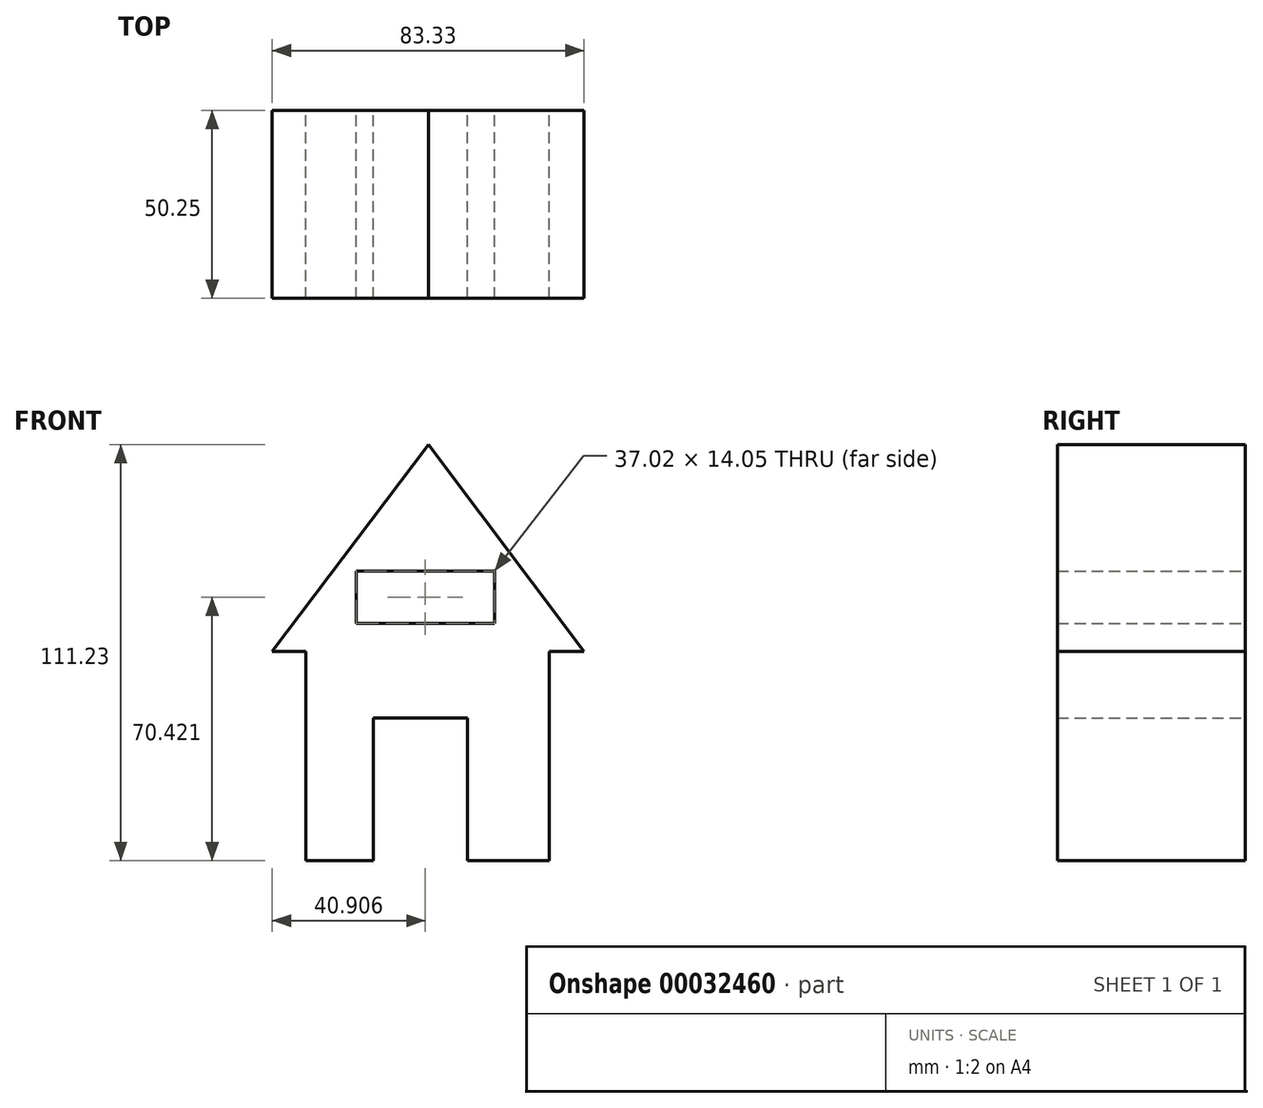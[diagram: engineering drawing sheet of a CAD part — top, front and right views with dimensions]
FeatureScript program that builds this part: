
annotation { "Feature Type Name" : "Feature", "Feature Type Description" : "" }
export const myFeature = defineFeature(function(context is Context, id is Id, definition is map)
    precondition{}
    {
        {
            var Q0;
            Q0=qCreatedBy(makeId("Front.planeOp"),FACE);
            var sketch = newSketch(context, id + "F0", { "sketchPlane" : qUnion([Q0])});
            skLineSegment(sketch, "E0.bottom", {"start": v(-32.84, 0) * mm, "end": v(32.27, 0) * mm});
            skLineSegment(sketch, "E0.top", {"start": v(-32.84, -55.9) * mm, "end": v(32.27, -55.9) * mm});
            skLineSegment(sketch, "E0.left", {"start": v(-32.84, 0) * mm, "end": v(-32.84, -55.9) * mm});
            skLineSegment(sketch, "E0.right", {"start": v(32.27, 0) * mm, "end": v(32.27, -55.9) * mm});
            skLineSegment(sketch, "E1", {"start": v(-41.76, 0) * mm, "end": v(41.57, 0) * mm});
            skLineSegment(sketch, "E2", {"start": v(-41.76, 0) * mm, "end": v(0, 55.33) * mm});
            skLineSegment(sketch, "E3", {"start": v(41.57, 0) * mm, "end": v(0, 55.33) * mm});
            skLineSegment(sketch, "E4", {"start": v(-14.8, -55.9) * mm, "end": v(-14.8, -17.75) * mm});
            skLineSegment(sketch, "E5", {"start": v(-14.8, -17.75) * mm, "end": v(10.44, -17.75) * mm});
            skLineSegment(sketch, "E6", {"start": v(10.44, -17.75) * mm, "end": v(10.44, -55.9) * mm});
            skLineSegment(sketch, "E7.bottom", {"start": v(-19.36, 21.54) * mm, "end": v(17.65, 21.54) * mm});
            skLineSegment(sketch, "E7.top", {"start": v(-19.36, 7.5) * mm, "end": v(17.65, 7.5) * mm});
            skLineSegment(sketch, "E7.left", {"start": v(-19.36, 21.54) * mm, "end": v(-19.36, 7.5) * mm});
            skLineSegment(sketch, "E7.right", {"start": v(17.65, 21.54) * mm, "end": v(17.65, 7.5) * mm});
            skSolve(sketch);
        }
        {
            var Q0;
            {var subQ1=sQuery(id+"F0.wireOp",EDGE,"E2");Q0=makeQuery(id+"F0.imprint","IMPRINT",FACE,{"disambiguationData":[TD([[makeQuery(id+"F0.imprint","IMPRINT",EDGE,{"derivedFrom":subQ1}),-1.0]])]});}
            var Q1;
            {var subQ3=sQuery(id+"F0.wireOp",EDGE,"E0.left");Q1=makeQuery(id+"F0.imprint","IMPRINT",FACE,{"disambiguationData":[TD([[makeQuery(id+"F0.imprint","IMPRINT",EDGE,{"derivedFrom":subQ3}),1.0]])]});}
            extrude(context, id + "F1", {"entities" : qUnion([Q0, Q1]), "depth" : 50.25 * mm});
        }
    });
